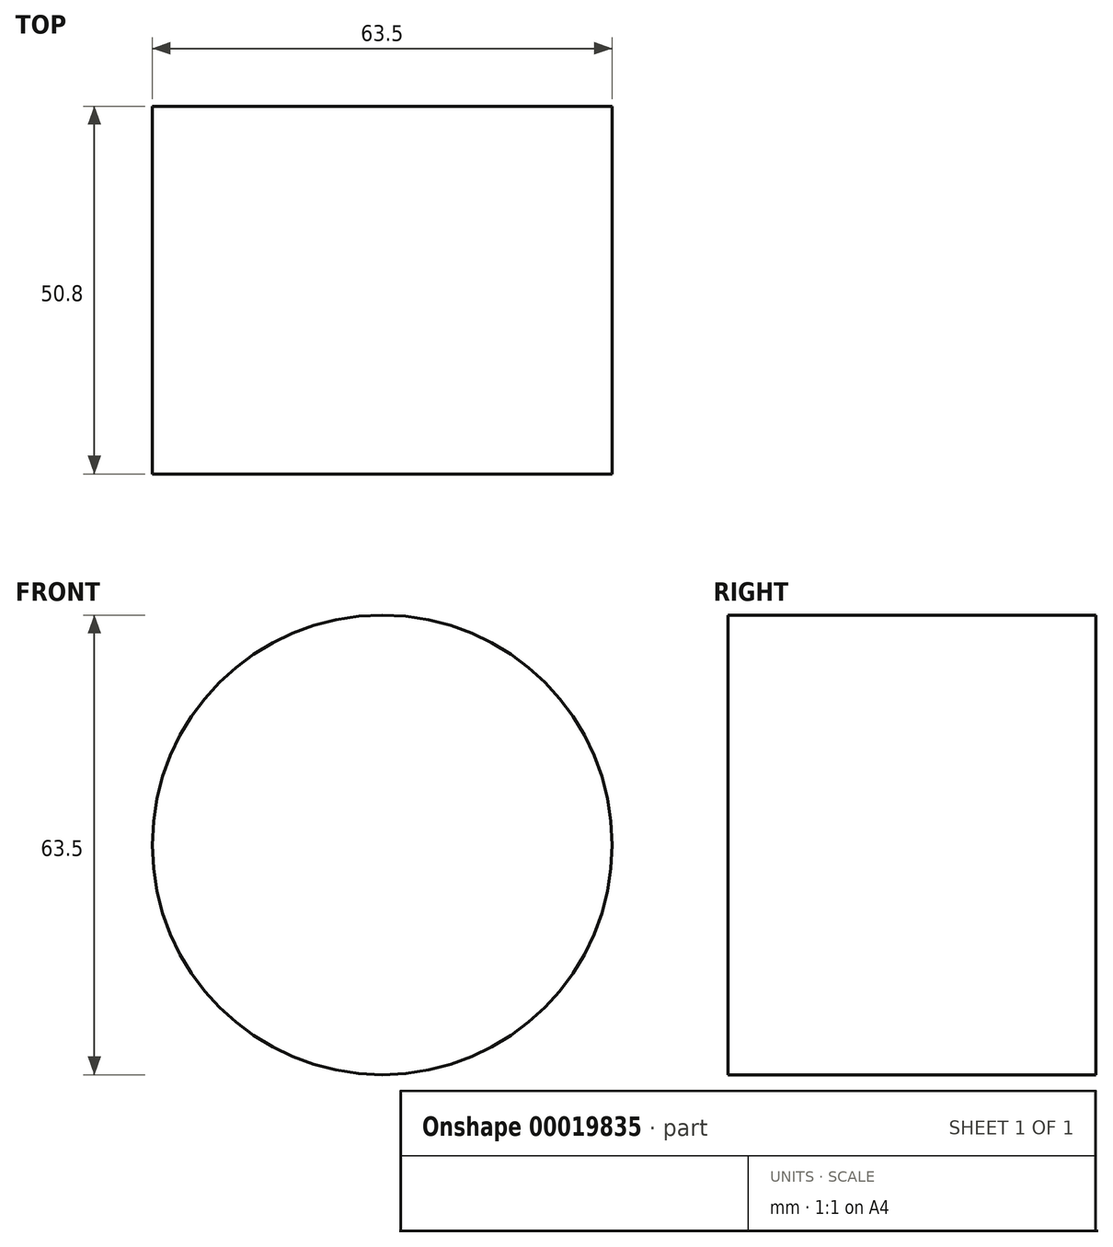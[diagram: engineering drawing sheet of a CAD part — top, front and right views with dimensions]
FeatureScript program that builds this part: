
annotation { "Feature Type Name" : "Feature", "Feature Type Description" : "" }
export const myFeature = defineFeature(function(context is Context, id is Id, definition is map)
    precondition{}
    {
        {
            var Q0;
            Q0=qCreatedBy(makeId("Front.planeOp"),FACE);
            var sketch = newSketch(context, id + "F0", { "sketchPlane" : qUnion([Q0])});
            skCircle(sketch, "E0", {"center": v(0, 0) * mm, "radius": 31.75 * mm});
            skSolve(sketch);
        }
        {
            var Q0;
            Q0 = qSketchRegion(id + "F0", true);
            var Q1;
            Q1=makeQuery(id+"F0.imprint","IMPRINT",FACE,{"disambiguationData":[TD([[makeQuery(id+"F0.imprint","IMPRINT",EDGE,{"derivedFrom":sQuery(id+"F0.wireOp",EDGE,"E0")}),1.0]])]});
            extrude(context, id + "F1", {"entities" : qUnion([Q0, Q1]), "depth" : 50.8 * mm});
        }
    });
